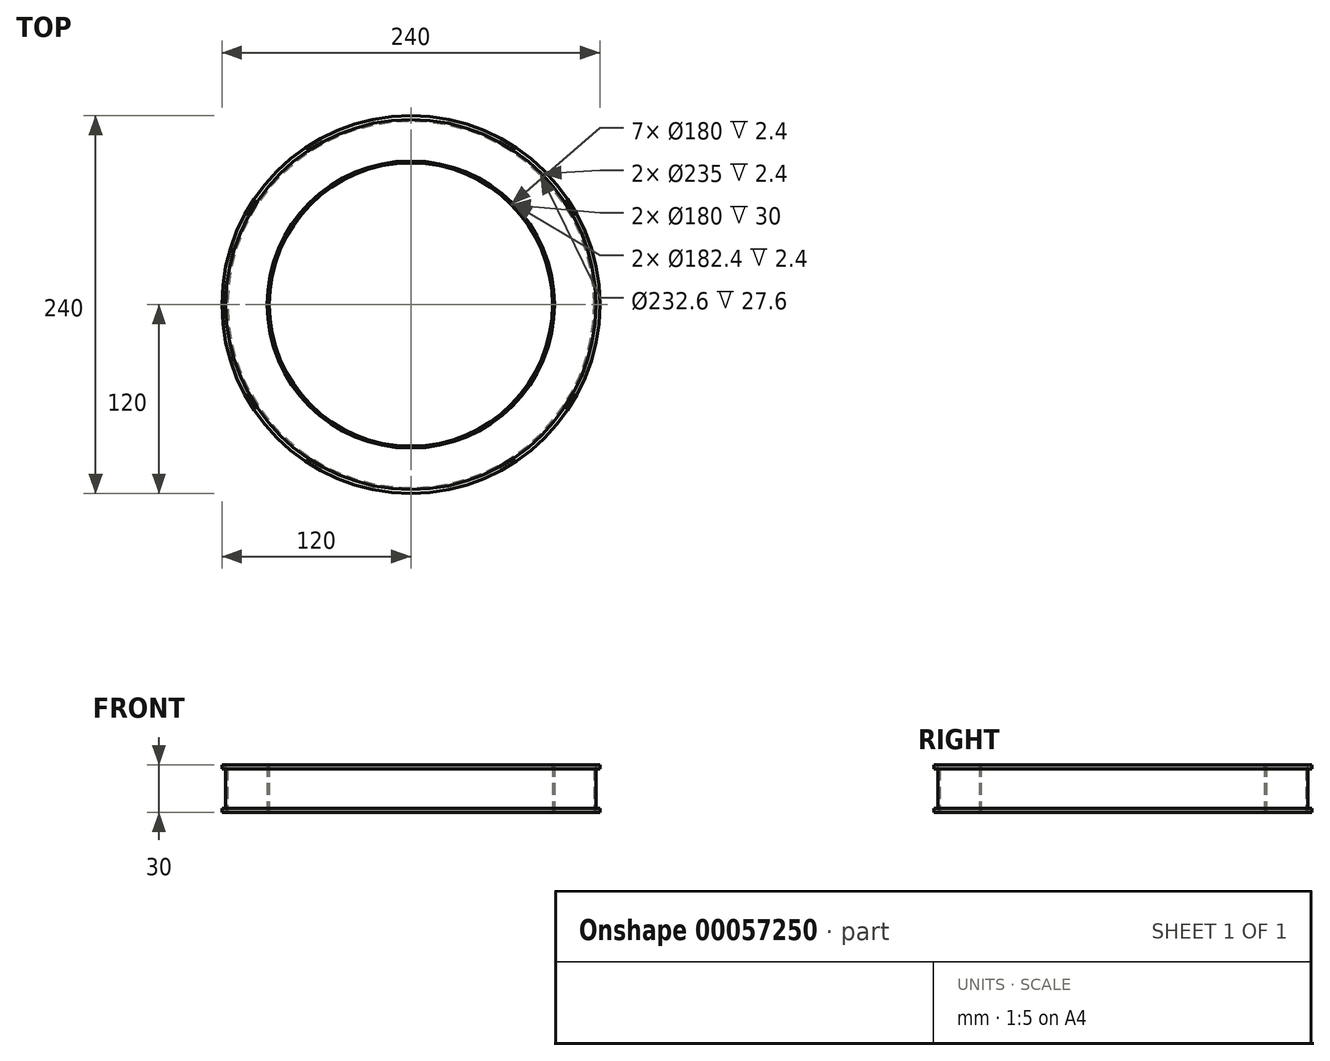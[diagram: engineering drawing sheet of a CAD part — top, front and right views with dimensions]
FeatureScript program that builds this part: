
annotation { "Feature Type Name" : "Feature", "Feature Type Description" : "" }
export const myFeature = defineFeature(function(context is Context, id is Id, definition is map)
    precondition{}
    {
        {
            var Q0;
            Q0=qCreatedBy(makeId("Top.planeOp"),FACE);
            var sketch = newSketch(context, id + "F0", { "sketchPlane" : qUnion([Q0])});
            skCircle(sketch, "E0", {"center": v(0, 0) * mm, "radius": 120 * mm});
            skCircle(sketch, "E1", {"center": v(0, 0) * mm, "radius": 90 * mm});
            skCircle(sketch, "E2", {"center": v(0, 0) * mm, "radius": 91.2 * mm});
            skCircle(sketch, "E3", {"center": v(0, 0) * mm, "radius": 116.3 * mm});
            skCircle(sketch, "E4", {"center": v(0, 0) * mm, "radius": 117.5 * mm});
            skSolve(sketch);
        }
        {
            var Q0;
            Q0=makeQuery(id+"F0.imprint","IMPRINT",FACE,{"disambiguationData":[TD([[makeQuery(id+"F0.imprint","IMPRINT",EDGE,{"derivedFrom":sQuery(id+"F0.wireOp",EDGE,"E1")}),-1.0]])]});
            extrude(context, id + "F1", {"entities" : qUnion([Q0]), "depth" : 30 * mm});
        }
        {
            var Q0;
            Q0=makeQuery(id+"F0.imprint","IMPRINT",FACE,{"disambiguationData":[TD([[makeQuery(id+"F0.imprint","IMPRINT",EDGE,{"derivedFrom":sQuery(id+"F0.wireOp",EDGE,"E3")}),-1.0]])]});
            extrude(context, id + "F2", {"entities" : qUnion([Q0]), "depth" : 30 * mm});
        }
        {
            var Q0;
            Q0=makeQuery(id+"F0.imprint","IMPRINT",FACE,{"disambiguationData":[TD([[makeQuery(id+"F0.imprint","IMPRINT",EDGE,{"derivedFrom":sQuery(id+"F0.wireOp",EDGE,"E2")}),-1.0]])]});
            var Q1;
            Q1=makeQuery(id+"F0.imprint","IMPRINT",FACE,{"disambiguationData":[TD([[makeQuery(id+"F0.imprint","IMPRINT",EDGE,{"derivedFrom":sQuery(id+"F0.wireOp",EDGE,"E0")}),1.0]])]});
            extrude(context, id + "F3", {"entities" : qUnion([Q0, Q1]), "depth" : 2.4 * mm});
        }
        {
            var Q0;
            Q0=makeQuery(id+"F2.opExtrude","CAP_FACE",FACE,{"disambiguationData":[OSD([sQuery(id+"F0.wireOp",EDGE,"E3"),sQuery(id+"F0.wireOp",EDGE,"E4")])],"isStart":false});
            var sketch = newSketch(context, id + "F4", { "sketchPlane" : qUnion([Q0])});
            skCircle(sketch, "E5", {"center": v(0, 0) * mm, "radius": 120 * mm});
            skCircle(sketch, "E6", {"center": v(0, 0) * mm, "radius": 116.3 * mm});
            skLineSegment(sketch, "E7.rect.bottom", {"start": v(-116.22, 4.28) * mm, "end": v(116.22, 4.28) * mm});
            skLineSegment(sketch, "E7.rect.top", {"start": v(-116.22, -4.28) * mm, "end": v(116.22, -4.28) * mm});
            skLineSegment(sketch, "E8.rect.bottom", {"start": v(-119.92, 4.28) * mm, "end": v(-112.52, 4.28) * mm});
            skLineSegment(sketch, "E8.rect.top", {"start": v(-119.92, 4.28) * mm, "end": v(-112.52, 4.28) * mm});
            skLineSegment(sketch, "E8.rect.left", {"start": v(-119.92, 4.28) * mm, "end": v(-119.92, 4.28) * mm});
            skLineSegment(sketch, "E8.rect.right", {"start": v(-112.52, 4.28) * mm, "end": v(-112.52, 4.28) * mm});
            skPoint(sketch, "E8.rect.middle", {"position": v(-116.22, 4.28) * mm});
            skLineSegment(sketch, "E9.rect.bottom", {"start": v(-119.92, -4.28) * mm, "end": v(-112.52, -4.28) * mm});
            skLineSegment(sketch, "E9.rect.top", {"start": v(-119.92, -4.28) * mm, "end": v(-112.52, -4.28) * mm});
            skLineSegment(sketch, "E9.rect.left", {"start": v(-119.92, -4.28) * mm, "end": v(-119.92, -4.28) * mm});
            skLineSegment(sketch, "E9.rect.right", {"start": v(-112.52, -4.28) * mm, "end": v(-112.52, -4.28) * mm});
            skPoint(sketch, "E9.rect.middle", {"position": v(-116.22, -4.28) * mm});
            skLineSegment(sketch, "E10.rect.bottom", {"start": v(119.92, 4.28) * mm, "end": v(112.52, 4.28) * mm});
            skLineSegment(sketch, "E10.rect.top", {"start": v(119.92, 4.28) * mm, "end": v(112.52, 4.28) * mm});
            skLineSegment(sketch, "E10.rect.left", {"start": v(119.92, 4.28) * mm, "end": v(119.92, 4.28) * mm});
            skLineSegment(sketch, "E10.rect.right", {"start": v(112.52, 4.28) * mm, "end": v(112.52, 4.28) * mm});
            skPoint(sketch, "E10.rect.middle", {"position": v(116.22, 4.28) * mm});
            skLineSegment(sketch, "E11.rect.bottom", {"start": v(119.92, -4.28) * mm, "end": v(112.52, -4.28) * mm});
            skLineSegment(sketch, "E11.rect.top", {"start": v(119.92, -4.28) * mm, "end": v(112.52, -4.28) * mm});
            skLineSegment(sketch, "E11.rect.left", {"start": v(119.92, -4.28) * mm, "end": v(119.92, -4.28) * mm});
            skLineSegment(sketch, "E11.rect.right", {"start": v(112.52, -4.28) * mm, "end": v(112.52, -4.28) * mm});
            skCircle(sketch, "E12", {"center": v(0, 0) * mm, "radius": 90 * mm});
            skSolve(sketch);
        }
        {
            var Q0;
            Q0 = qSketchRegion(id + "F4", true);
            extrude(context, id + "F5", {"entities" : qUnion([Q0]), "operationType" : NewBodyOperationType.ADD, "oppositeDirection" : true, "depth" : 2.4 * mm});
        }
        {
            var Q0;
            {var subQ0=sQuery(id+"F4.wireOp",EDGE,"E10.rect.top");var subQ5=sQuery(id+"F4.wireOp",EDGE,"E6");var subQ6=makeQuery(id+"F4.imprint","INTERSECT",VERTEX,{"derivedFrom":[subQ5,subQ0]});Q0=makeQuery(id+"F4.imprint","IMPRINT",FACE,{"disambiguationData":[TD([[makeQuery(id+"F4.imprint","IMPRINT",EDGE,{"disambiguationData":[TD([[subQ6,1.0]])],"derivedFrom":subQ5}),1.0]])]});}
            var Q1;
            {var subQ0=sQuery(id+"F4.wireOp",EDGE,"E10.rect.top");var subQ1=sQuery(id+"F4.wireOp",EDGE,"E6");var subQ2=makeQuery(id+"F4.imprint","INTERSECT",VERTEX,{"derivedFrom":[subQ1,subQ0]});Q1=makeQuery(id+"F4.imprint","IMPRINT",FACE,{"disambiguationData":[TD([[makeQuery(id+"F4.imprint","IMPRINT",EDGE,{"disambiguationData":[TD([[subQ2,1.0]])],"derivedFrom":subQ1}),-1.0]])]});}
            var Q2;
            {var subQ5=sQuery(id+"F4.wireOp",EDGE,"E8.rect.top");var subQ9=sQuery(id+"F4.wireOp",EDGE,"E6");var subQ10=makeQuery(id+"F4.imprint","INTERSECT",VERTEX,{"derivedFrom":[subQ9,subQ5]});Q2=makeQuery(id+"F4.imprint","IMPRINT",FACE,{"disambiguationData":[TD([[makeQuery(id+"F4.imprint","IMPRINT",EDGE,{"disambiguationData":[TD([[subQ10,-1.0]])],"derivedFrom":subQ9}),1.0]])]});}
            var Q3;
            {var subQ0=sQuery(id+"F4.wireOp",EDGE,"E8.rect.top");var subQ1=sQuery(id+"F4.wireOp",EDGE,"E6");var subQ2=makeQuery(id+"F4.imprint","INTERSECT",VERTEX,{"derivedFrom":[subQ1,subQ0]});Q3=makeQuery(id+"F4.imprint","IMPRINT",FACE,{"disambiguationData":[TD([[makeQuery(id+"F4.imprint","IMPRINT",EDGE,{"disambiguationData":[TD([[subQ2,-1.0]])],"derivedFrom":subQ1}),-1.0]])]});}
            extrude(context, id + "F6", {"entities" : qUnion([Q0, Q1, Q2, Q3]), "oppositeDirection" : true, "depth" : 2.4 * mm});
        }
        {
            var Q0;
            Q0=makeQuery(id+"F6.opExtrude","SWEPT_BODY",BODY,{"disambiguationData":[OSD([sQuery(id+"F0.wireOp",EDGE,"E4"),sQuery(id+"F4.wireOp",EDGE,"E7.rect.bottom"),sQuery(id+"F4.wireOp",EDGE,"E7.rect.top"),sQuery(id+"F4.wireOp",EDGE,"E8.rect.top"),sQuery(id+"F4.wireOp",EDGE,"E9.rect.top"),sQuery(id+"F4.wireOp",EDGE,"E12")])]});
            var Q1;
            Q1=makeQuery(id+"F6.opExtrude","SWEPT_BODY",BODY,{"disambiguationData":[OSD([sQuery(id+"F0.wireOp",EDGE,"E4"),sQuery(id+"F4.wireOp",EDGE,"E7.rect.bottom"),sQuery(id+"F4.wireOp",EDGE,"E7.rect.top"),sQuery(id+"F4.wireOp",EDGE,"E10.rect.top"),sQuery(id+"F4.wireOp",EDGE,"E11.rect.top"),sQuery(id+"F4.wireOp",EDGE,"E12")])]});
            var Q2;
            Q2=sQuery(id+"F4.wireOp",EDGE,"E6");
            transform(context, id + "F7", {"entities" : qUnion([Q0, Q1]), "transformType" : TransformType.ROTATION, "transformAxis" : qUnion([Q2]), "angle" : 20 * degree, "makeCopy" : true});
        }
        {
            var Q0;
            Q0=makeQuery(id+"F7.opPattern","COPY",BODY,{"derivedFrom":makeQuery(id+"F6.opExtrude","SWEPT_BODY",BODY,{"disambiguationData":[OSD([sQuery(id+"F0.wireOp",EDGE,"E4"),sQuery(id+"F4.wireOp",EDGE,"E7.rect.bottom"),sQuery(id+"F4.wireOp",EDGE,"E7.rect.top"),sQuery(id+"F4.wireOp",EDGE,"E8.rect.top"),sQuery(id+"F4.wireOp",EDGE,"E9.rect.top"),sQuery(id+"F4.wireOp",EDGE,"E12")])]}),"instanceName":"1"});
            var Q1;
            Q1=makeQuery(id+"F7.opPattern","COPY",BODY,{"derivedFrom":makeQuery(id+"F6.opExtrude","SWEPT_BODY",BODY,{"disambiguationData":[OSD([sQuery(id+"F0.wireOp",EDGE,"E4"),sQuery(id+"F4.wireOp",EDGE,"E7.rect.bottom"),sQuery(id+"F4.wireOp",EDGE,"E7.rect.top"),sQuery(id+"F4.wireOp",EDGE,"E10.rect.top"),sQuery(id+"F4.wireOp",EDGE,"E11.rect.top"),sQuery(id+"F4.wireOp",EDGE,"E12")])]}),"instanceName":"1"});
            var Q2;
            Q2=sQuery(id+"F4.wireOp",EDGE,"E6");
            transform(context, id + "F8", {"entities" : qUnion([Q0, Q1]), "transformType" : TransformType.ROTATION, "transformAxis" : qUnion([Q2]), "angle" : 20 * degree, "makeCopy" : true});
        }
        {
            var Q0;
            Q0=makeQuery(id+"F6.opExtrude","SWEPT_BODY",BODY,{"disambiguationData":[OSD([sQuery(id+"F0.wireOp",EDGE,"E4"),sQuery(id+"F4.wireOp",EDGE,"E7.rect.bottom"),sQuery(id+"F4.wireOp",EDGE,"E7.rect.top"),sQuery(id+"F4.wireOp",EDGE,"E8.rect.top"),sQuery(id+"F4.wireOp",EDGE,"E9.rect.top"),sQuery(id+"F4.wireOp",EDGE,"E12")])]});
            var Q1;
            Q1=makeQuery(id+"F7.opPattern","COPY",BODY,{"derivedFrom":makeQuery(id+"F6.opExtrude","SWEPT_BODY",BODY,{"disambiguationData":[OSD([sQuery(id+"F0.wireOp",EDGE,"E4"),sQuery(id+"F4.wireOp",EDGE,"E7.rect.bottom"),sQuery(id+"F4.wireOp",EDGE,"E7.rect.top"),sQuery(id+"F4.wireOp",EDGE,"E8.rect.top"),sQuery(id+"F4.wireOp",EDGE,"E9.rect.top"),sQuery(id+"F4.wireOp",EDGE,"E12")])]}),"instanceName":"1"});
            var Q2;
            Q2=makeQuery(id+"F8.opPattern","COPY",BODY,{"derivedFrom":makeQuery(id+"F7.opPattern","COPY",BODY,{"derivedFrom":makeQuery(id+"F6.opExtrude","SWEPT_BODY",BODY,{"disambiguationData":[OSD([sQuery(id+"F0.wireOp",EDGE,"E4"),sQuery(id+"F4.wireOp",EDGE,"E7.rect.bottom"),sQuery(id+"F4.wireOp",EDGE,"E7.rect.top"),sQuery(id+"F4.wireOp",EDGE,"E8.rect.top"),sQuery(id+"F4.wireOp",EDGE,"E9.rect.top"),sQuery(id+"F4.wireOp",EDGE,"E12")])]}),"instanceName":"1"}),"instanceName":"1"});
            var Q3;
            Q3=makeQuery(id+"F6.opExtrude","SWEPT_BODY",BODY,{"disambiguationData":[OSD([sQuery(id+"F0.wireOp",EDGE,"E4"),sQuery(id+"F4.wireOp",EDGE,"E7.rect.bottom"),sQuery(id+"F4.wireOp",EDGE,"E7.rect.top"),sQuery(id+"F4.wireOp",EDGE,"E10.rect.top"),sQuery(id+"F4.wireOp",EDGE,"E11.rect.top"),sQuery(id+"F4.wireOp",EDGE,"E12")])]});
            var Q4;
            Q4=makeQuery(id+"F7.opPattern","COPY",BODY,{"derivedFrom":makeQuery(id+"F6.opExtrude","SWEPT_BODY",BODY,{"disambiguationData":[OSD([sQuery(id+"F0.wireOp",EDGE,"E4"),sQuery(id+"F4.wireOp",EDGE,"E7.rect.bottom"),sQuery(id+"F4.wireOp",EDGE,"E7.rect.top"),sQuery(id+"F4.wireOp",EDGE,"E10.rect.top"),sQuery(id+"F4.wireOp",EDGE,"E11.rect.top"),sQuery(id+"F4.wireOp",EDGE,"E12")])]}),"instanceName":"1"});
            var Q5;
            Q5=makeQuery(id+"F8.opPattern","COPY",BODY,{"derivedFrom":makeQuery(id+"F7.opPattern","COPY",BODY,{"derivedFrom":makeQuery(id+"F6.opExtrude","SWEPT_BODY",BODY,{"disambiguationData":[OSD([sQuery(id+"F0.wireOp",EDGE,"E4"),sQuery(id+"F4.wireOp",EDGE,"E7.rect.bottom"),sQuery(id+"F4.wireOp",EDGE,"E7.rect.top"),sQuery(id+"F4.wireOp",EDGE,"E10.rect.top"),sQuery(id+"F4.wireOp",EDGE,"E11.rect.top"),sQuery(id+"F4.wireOp",EDGE,"E12")])]}),"instanceName":"1"}),"instanceName":"1"});
            var Q6;
            Q6=sQuery(id+"F4.wireOp",EDGE,"E6");
            transform(context, id + "F9", {"entities" : qUnion([Q0, Q1, Q2, Q3, Q4, Q5]), "transformType" : TransformType.ROTATION, "transformAxis" : qUnion([Q6]), "angle" : 60 * degree, "makeCopy" : true});
        }
    });
